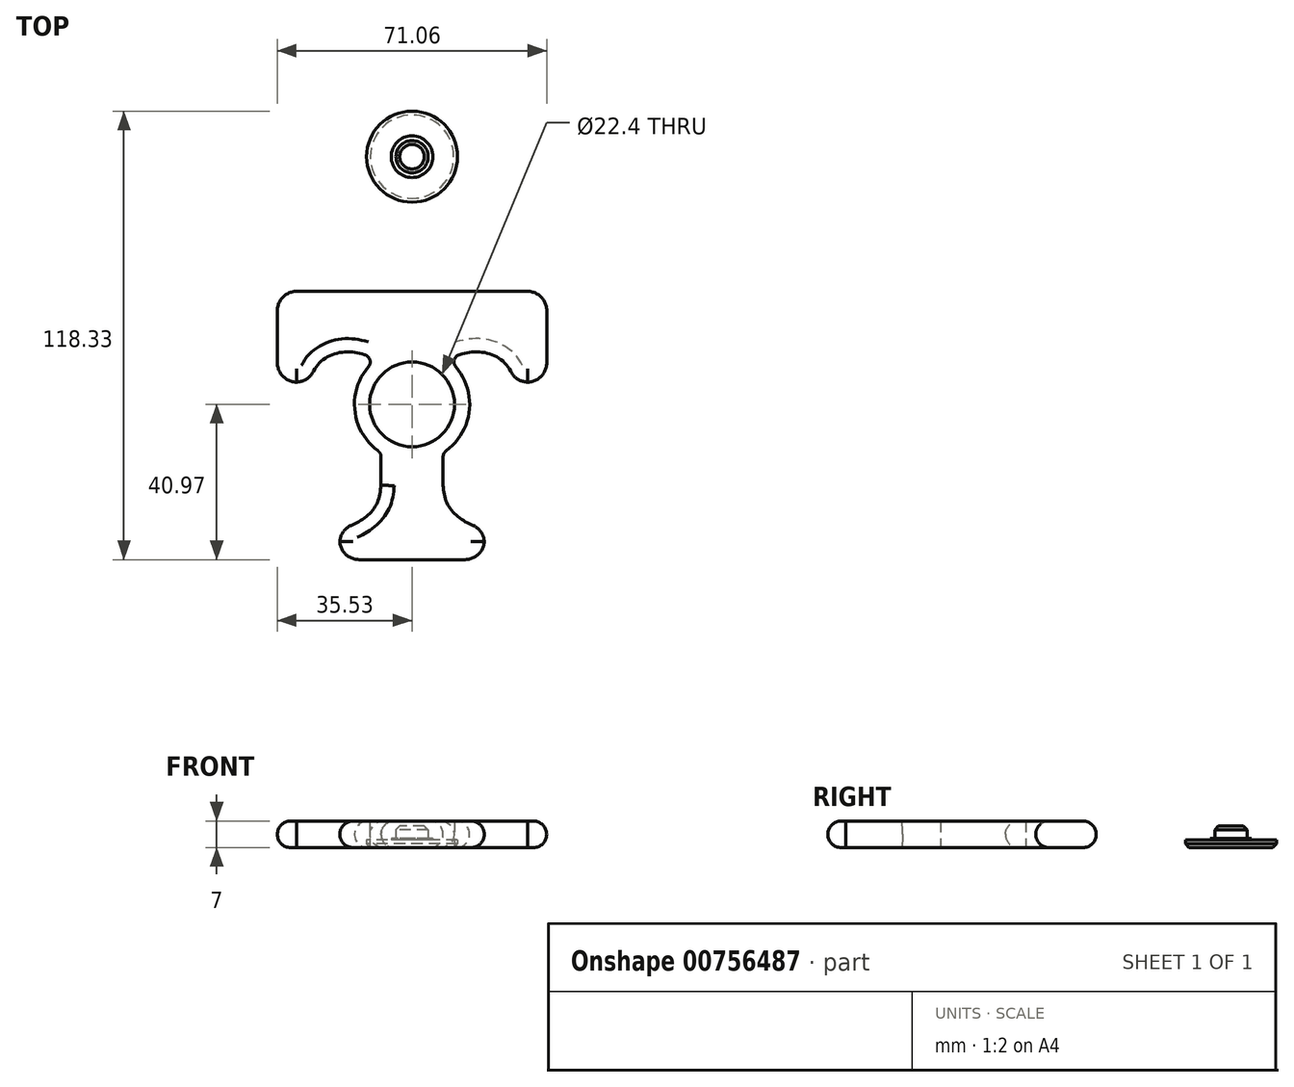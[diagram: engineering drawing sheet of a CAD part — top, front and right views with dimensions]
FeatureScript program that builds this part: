
annotation { "Feature Type Name" : "Feature", "Feature Type Description" : "" }
export const myFeature = defineFeature(function(context is Context, id is Id, definition is map)
    precondition{}
    {
        {
            var Q0;
            Q0=qCreatedBy(makeId("Top.planeOp"),FACE);
            var sketch = newSketch(context, id + "F0", { "sketchPlane" : qUnion([Q0])});
            skCircle(sketch, "E0", {"center": v(0, 0) * mm, "radius": 11.2 * mm});
            skArc(sketch, "E1.0", {"start": v(-9.62, 11.77) * mm, "mid": v(-15.17, -0.88) * mm, "end": v(-8.19, -12.8) * mm});
            skLineSegment(sketch, "E2", {"start": v(-19.07, -40.97) * mm, "end": v(19.07, -40.97) * mm});
            skLineSegment(sketch, "E3", {"start": v(19.07, -40.97) * mm, "end": v(19.07, -32.32) * mm});
            skLineSegment(sketch, "E4", {"start": v(-19.07, -40.97) * mm, "end": v(-19.07, -32.32) * mm});
            skLineSegment(sketch, "E5", {"start": v(-8.19, -12.8) * mm, "end": v(-8.19, -21.28) * mm});
            skFitSpline(sketch, "E6", {"points": [v(-8.19, -21.28) * mm, v(-8.77, -24.86) * mm, v(-10.64, -28.2) * mm, v(-13.4, -30.57) * mm, v(-15.96, -31.85) * mm, v(-19.07, -32.32) * mm], "startDerivative": vector(-2.1, -18.08) * mm, "endDerivative": vector(-16.92, -1.44) * mm});
            skLineSegment(sketch, "E7.MirrorCS", {"start": v(8.19, -12.8) * mm, "end": v(8.19, -21.28) * mm});
            skFitSpline(sketch, "E8.MirrorCS", {"points": [v(8.19, -21.28) * mm, v(8.77, -24.86) * mm, v(10.64, -28.2) * mm, v(13.4, -30.57) * mm, v(15.96, -31.85) * mm, v(19.07, -32.32) * mm], "startDerivative": vector(2.1, -18.08) * mm, "endDerivative": vector(16.92, -1.44) * mm});
            skLineSegment(sketch, "E9", {"start": v(26.74, 5.88) * mm, "end": v(35.53, 5.88) * mm});
            skLineSegment(sketch, "E10", {"start": v(35.53, 5.88) * mm, "end": v(35.53, 29.84) * mm});
            skLineSegment(sketch, "E11", {"start": v(35.53, 29.84) * mm, "end": v(-35.53, 29.84) * mm});
            skLineSegment(sketch, "E12", {"start": v(-35.53, 29.84) * mm, "end": v(-35.53, 5.88) * mm});
            skLineSegment(sketch, "E13", {"start": v(-35.53, 5.88) * mm, "end": v(-26.74, 5.88) * mm});
            skFitSpline(sketch, "E14", {"points": [v(-26.74, 5.88) * mm, v(-26.56, 7.22) * mm, v(-26.03, 8.7) * mm, v(-25.04, 10.28) * mm, v(-23.42, 11.81) * mm, v(-21.16, 13.08) * mm, v(-18.2, 13.8) * mm, v(-15.67, 13.78) * mm, v(-13.62, 13.4) * mm, v(-11.93, 12.94) * mm, v(-10.86, 12.51) * mm, v(-10.1, 12.13) * mm, v(-9.62, 11.77) * mm], "startDerivative": vector(1.87, 19.05) * mm, "endDerivative": vector(10.83, -14.58) * mm});
            skFitSpline(sketch, "E15.MirrorCS", {"points": [v(26.74, 5.88) * mm, v(26.56, 7.22) * mm, v(26.03, 8.7) * mm, v(25.04, 10.28) * mm, v(23.42, 11.81) * mm, v(21.16, 13.08) * mm, v(18.2, 13.8) * mm, v(15.67, 13.78) * mm, v(13.62, 13.4) * mm, v(11.93, 12.94) * mm, v(10.86, 12.51) * mm, v(10.1, 12.13) * mm, v(9.62, 11.77) * mm], "startDerivative": vector(-1.87, 19.05) * mm, "endDerivative": vector(-10.83, -14.58) * mm});
            skLineSegment(sketch, "E16.trimOffspring", {"start": v(9.62, 11.77) * mm, "end": v(9.62, 11.77) * mm});
            skArc(sketch, "E17.trimOffspring", {"start": v(8.19, -12.8) * mm, "mid": v(15.17, -0.88) * mm, "end": v(9.62, 11.77) * mm});
            skPoint(sketch, "E18.orphan", {"position": v(8.19, -10.35) * mm});
            skPoint(sketch, "E19.orphan", {"position": v(-8.19, -10.35) * mm});
            skSolve(sketch);
        }
        {
            var Q0;
            Q0 = qSketchRegion(id + "F0", true);
            var Q1;
            Q1=makeQuery(id+"F0.imprint","IMPRINT",FACE,{"disambiguationData":[TD([[makeQuery(id+"F0.imprint","IMPRINT",EDGE,{"derivedFrom":sQuery(id+"F0.wireOp",EDGE,"E0")}),1.0]])]});
            extrude(context, id + "F1", {"entities" : qUnion([Q0, Q1]), "flatOperationType" : FlatOperationType.REMOVE, "thickness1" : 5 * mm, "thickness2" : 0 * mm, "thickness" : 5 * mm, "depth" : 7 * mm, "offsetDistance" : 25.4 * mm, "startOffsetBound" : StartOffsetType.BLIND, "startOffsetDistance" : 25 * mm, "domain" : OperationDomain.MODEL});
        }
        {
            var Q0;
            Q0=makeQuery(id+"F1.opExtrude","SWEPT_EDGE",EDGE,{"disambiguationData":[OSD([sQuery(id+"F0.wireOp",EDGE,"E11"),sQuery(id+"F0.wireOp",EDGE,"E12")])]});
            var Q1;
            Q1=makeQuery(id+"F1.opExtrude","SWEPT_EDGE",EDGE,{"disambiguationData":[OSD([sQuery(id+"F0.wireOp",EDGE,"E10"),sQuery(id+"F0.wireOp",EDGE,"E11")])]});
            var Q2;
            Q2=makeQuery(id+"F1.opExtrude","SWEPT_EDGE",EDGE,{"disambiguationData":[OSD([sQuery(id+"F0.wireOp",EDGE,"E9"),sQuery(id+"F0.wireOp",EDGE,"E10")])]});
            var Q3;
            Q3=makeQuery(id+"F1.opExtrude","SWEPT_EDGE",EDGE,{"disambiguationData":[OSD([sQuery(id+"F0.wireOp",EDGE,"E2"),sQuery(id+"F0.wireOp",EDGE,"E3")])]});
            var Q4;
            Q4=makeQuery(id+"F1.opExtrude","SWEPT_EDGE",EDGE,{"disambiguationData":[OSD([sQuery(id+"F0.wireOp",EDGE,"E2"),sQuery(id+"F0.wireOp",EDGE,"E4")])]});
            var Q5;
            Q5=makeQuery(id+"F1.opExtrude","SWEPT_EDGE",EDGE,{"disambiguationData":[OSD([sQuery(id+"F0.wireOp",EDGE,"E4"),sQuery(id+"F0.wireOp",EDGE,"E6")])]});
            var Q6;
            Q6=makeQuery(id+"F1.opExtrude","SWEPT_EDGE",EDGE,{"disambiguationData":[OSD([sQuery(id+"F0.wireOp",EDGE,"E12"),sQuery(id+"F0.wireOp",EDGE,"E13")])]});
            var Q7;
            Q7=makeQuery(id+"F1.opExtrude","SWEPT_EDGE",EDGE,{"disambiguationData":[OSD([sQuery(id+"F0.wireOp",EDGE,"E13"),sQuery(id+"F0.wireOp",EDGE,"E14")])]});
            var Q8;
            Q8=makeQuery(id+"F1.opExtrude","SWEPT_EDGE",EDGE,{"disambiguationData":[OSD([sQuery(id+"F0.wireOp",EDGE,"E3"),sQuery(id+"F0.wireOp",EDGE,"E8.MirrorCS")])]});
            var Q9;
            Q9=makeQuery(id+"F1.opExtrude","SWEPT_EDGE",EDGE,{"disambiguationData":[OSD([sQuery(id+"F0.wireOp",EDGE,"E9"),sQuery(id+"F0.wireOp",EDGE,"E15.MirrorCS")])]});
            fillet(context, id + "F2", {"entities" : qUnion([Q0, Q1, Q2, Q3, Q4, Q5, Q6, Q7, Q8, Q9]), "radius" : 5.08 * mm, "tangentPropagation" : true, "allowEdgeOverflow" : false});
        }
        {
            var Q0;
            Q0=qCreatedBy(makeId("Top.planeOp"),FACE);
            var sketch = newSketch(context, id + "F3", { "sketchPlane" : qUnion([Q0])});
            skCircle(sketch, "E20", {"center": v(0, 65.36) * mm, "radius": 12 * mm});
            skSolve(sketch);
        }
        {
            var Q0;
            Q0 = qSketchRegion(id + "F3", true);
            extrude(context, id + "F4", {"entities" : qUnion([Q0]), "depth" : 2 * mm, "offsetDistance" : 25 * mm});
        }
        {
            var Q0;
            Q0=makeQuery(id+"F4.opExtrude","CAP_FACE",FACE,{"disambiguationData":[OSD([sQuery(id+"F3.wireOp",EDGE,"E20")])],"isStart":false});
            var sketch = newSketch(context, id + "F5", { "sketchPlane" : qUnion([Q0])});
            skCircle(sketch, "E21", {"center": v(0, 65.36) * mm, "radius": 5.5 * mm});
            skSolve(sketch);
        }
        {
            var Q0;
            Q0 = qSketchRegion(id + "F5", true);
            extrude(context, id + "F6", {"entities" : qUnion([Q0]), "operationType" : NewBodyOperationType.ADD, "depth" : .4 * mm, "offsetDistance" : 25 * mm});
        }
        {
            var Q0;
            Q0=makeQuery(id+"F6.opExtrude","CAP_FACE",FACE,{"disambiguationData":[OSD([sQuery(id+"F5.wireOp",EDGE,"E21")])],"isStart":false});
            var sketch = newSketch(context, id + "F7", { "sketchPlane" : qUnion([Q0])});
            skCircle(sketch, "E22", {"center": v(0, 65.36) * mm, "radius": 4.25 * mm});
            skSolve(sketch);
        }
        {
            var Q0;
            Q0 = qSketchRegion(id + "F7", true);
            extrude(context, id + "F8", {"entities" : qUnion([Q0]), "operationType" : NewBodyOperationType.ADD, "depth" : 3.25 * mm, "offsetDistance" : 25 * mm});
        }
        {
            var Q0;
            Q0=makeQuery(id+"F4.opExtrude","CAP_EDGE",EDGE,{"disambiguationData":[OSD([sQuery(id+"F3.wireOp",EDGE,"E20")])],"isStart":true});
            var Q1;
            Q1=makeQuery(id+"F8.opExtrude","CAP_EDGE",EDGE,{"disambiguationData":[OSD([sQuery(id+"F7.wireOp",EDGE,"E22")])],"isStart":false});
            chamfer(context, id + "F9", {"entities" : qUnion([Q0, Q1]), "width" : 1 * mm, "tangentPropagation" : true});
        }
        {
            var Q0;
            Q0=makeQuery(id+"F1.opExtrude","SWEPT_EDGE",EDGE,{"disambiguationData":[OSD([sQuery(id+"F0.wireOp",EDGE,"E15.MirrorCS"),sQuery(id+"F0.wireOp",EDGE,"E16.trimOffspring")])]});
            var Q1;
            Q1=makeQuery(id+"F1.opExtrude","SWEPT_EDGE",EDGE,{"disambiguationData":[OSD([sQuery(id+"F0.wireOp",EDGE,"E1.0"),sQuery(id+"F0.wireOp",EDGE,"E14")])]});
            var Q2;
            Q2=makeQuery(id+"F1.opExtrude","SWEPT_EDGE",EDGE,{"disambiguationData":[OSD([sQuery(id+"F0.wireOp",EDGE,"E1.0"),sQuery(id+"F0.wireOp",EDGE,"E5")])]});
            var Q3;
            Q3=makeQuery(id+"F1.opExtrude","SWEPT_EDGE",EDGE,{"disambiguationData":[OSD([sQuery(id+"F0.wireOp",EDGE,"E7.MirrorCS"),sQuery(id+"F0.wireOp",EDGE,"E16.trimOffspring")])]});
            fillet(context, id + "F10", {"entities" : qUnion([Q0, Q1, Q2, Q3]), "radius" : 2 * mm, "tangentPropagation" : true, "defaultsChanged" : false, "vertexSettings" : [], "allowEdgeOverflow" : false});
        }
        {
            var Q0;
            Q0=makeQuery(id+"F1.opExtrude","CAP_FACE",FACE,{"disambiguationData":[OSD([sQuery(id+"F0.wireOp",EDGE,"E0"),sQuery(id+"F0.wireOp",EDGE,"E1.0"),sQuery(id+"F0.wireOp",EDGE,"E2"),sQuery(id+"F0.wireOp",EDGE,"E3"),sQuery(id+"F0.wireOp",EDGE,"E4"),sQuery(id+"F0.wireOp",EDGE,"E5"),sQuery(id+"F0.wireOp",EDGE,"E6"),sQuery(id+"F0.wireOp",EDGE,"E7.MirrorCS"),sQuery(id+"F0.wireOp",EDGE,"E8.MirrorCS"),sQuery(id+"F0.wireOp",EDGE,"E9"),sQuery(id+"F0.wireOp",EDGE,"E10"),sQuery(id+"F0.wireOp",EDGE,"E11"),sQuery(id+"F0.wireOp",EDGE,"E12"),sQuery(id+"F0.wireOp",EDGE,"E13"),sQuery(id+"F0.wireOp",EDGE,"E14"),sQuery(id+"F0.wireOp",EDGE,"E15.MirrorCS"),sQuery(id+"F0.wireOp",EDGE,"E17.trimOffspring")])],"isStart":false});
            var Q1;
            Q1=makeQuery(id+"F1.opExtrude","CAP_FACE",FACE,{"disambiguationData":[OSD([sQuery(id+"F0.wireOp",EDGE,"E0"),sQuery(id+"F0.wireOp",EDGE,"E1.0"),sQuery(id+"F0.wireOp",EDGE,"E2"),sQuery(id+"F0.wireOp",EDGE,"E3"),sQuery(id+"F0.wireOp",EDGE,"E4"),sQuery(id+"F0.wireOp",EDGE,"E5"),sQuery(id+"F0.wireOp",EDGE,"E6"),sQuery(id+"F0.wireOp",EDGE,"E7.MirrorCS"),sQuery(id+"F0.wireOp",EDGE,"E8.MirrorCS"),sQuery(id+"F0.wireOp",EDGE,"E9"),sQuery(id+"F0.wireOp",EDGE,"E10"),sQuery(id+"F0.wireOp",EDGE,"E11"),sQuery(id+"F0.wireOp",EDGE,"E12"),sQuery(id+"F0.wireOp",EDGE,"E13"),sQuery(id+"F0.wireOp",EDGE,"E14"),sQuery(id+"F0.wireOp",EDGE,"E15.MirrorCS"),sQuery(id+"F0.wireOp",EDGE,"E17.trimOffspring")])],"isStart":true});
            fillet(context, id + "F11", {"entities" : qUnion([Q0, Q1]), "radius" : 3.5 * mm, "tangentPropagation" : true, "defaultsChanged" : false, "vertexSettings" : [], "allowEdgeOverflow" : false});
        }
        {
            var Q0;
            Q0=makeQuery(id+"F0.imprint","IMPRINT",FACE,{"disambiguationData":[TD([[makeQuery(id+"F0.imprint","IMPRINT",EDGE,{"derivedFrom":sQuery(id+"F0.wireOp",EDGE,"E0")}),1.0]])]});
            extrude(context, id + "F12", {"entities" : qUnion([Q0]), "operationType" : NewBodyOperationType.REMOVE, "depth" : 8 * mm, "offsetDistance" : 25 * mm});
        }
    });
